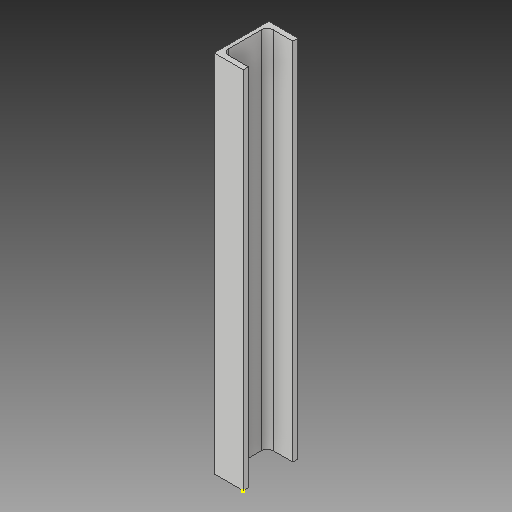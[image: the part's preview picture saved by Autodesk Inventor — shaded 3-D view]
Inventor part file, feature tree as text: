
AUTODESK INVENTOR PART (.ipt)
format: ipt  version: 2019 (Build 230136000, 136)  size: 93,184 bytes
history: native  units: in
note: dims shown in document units (in); Inventor stores cm internally (conversion verified against a paired STEP export)
features: other x3, sketch x2
ambient origin geometry x8: Origin, YZ Plane, XZ Plane, XY Plane, X Axis, Y Axis, Z Axis, Center Point
bodies: Solid1 (feature_tree)
feature tree (5):
  other  "Channel2_MIR2.ipt"
  other  "Solid1::Channel2_MIR2.ipt"
  other  "TaggingFeature1"
  sketch  "Sketch1"  dims[d0=0.3937in]
  sketch  "Sketch2"
